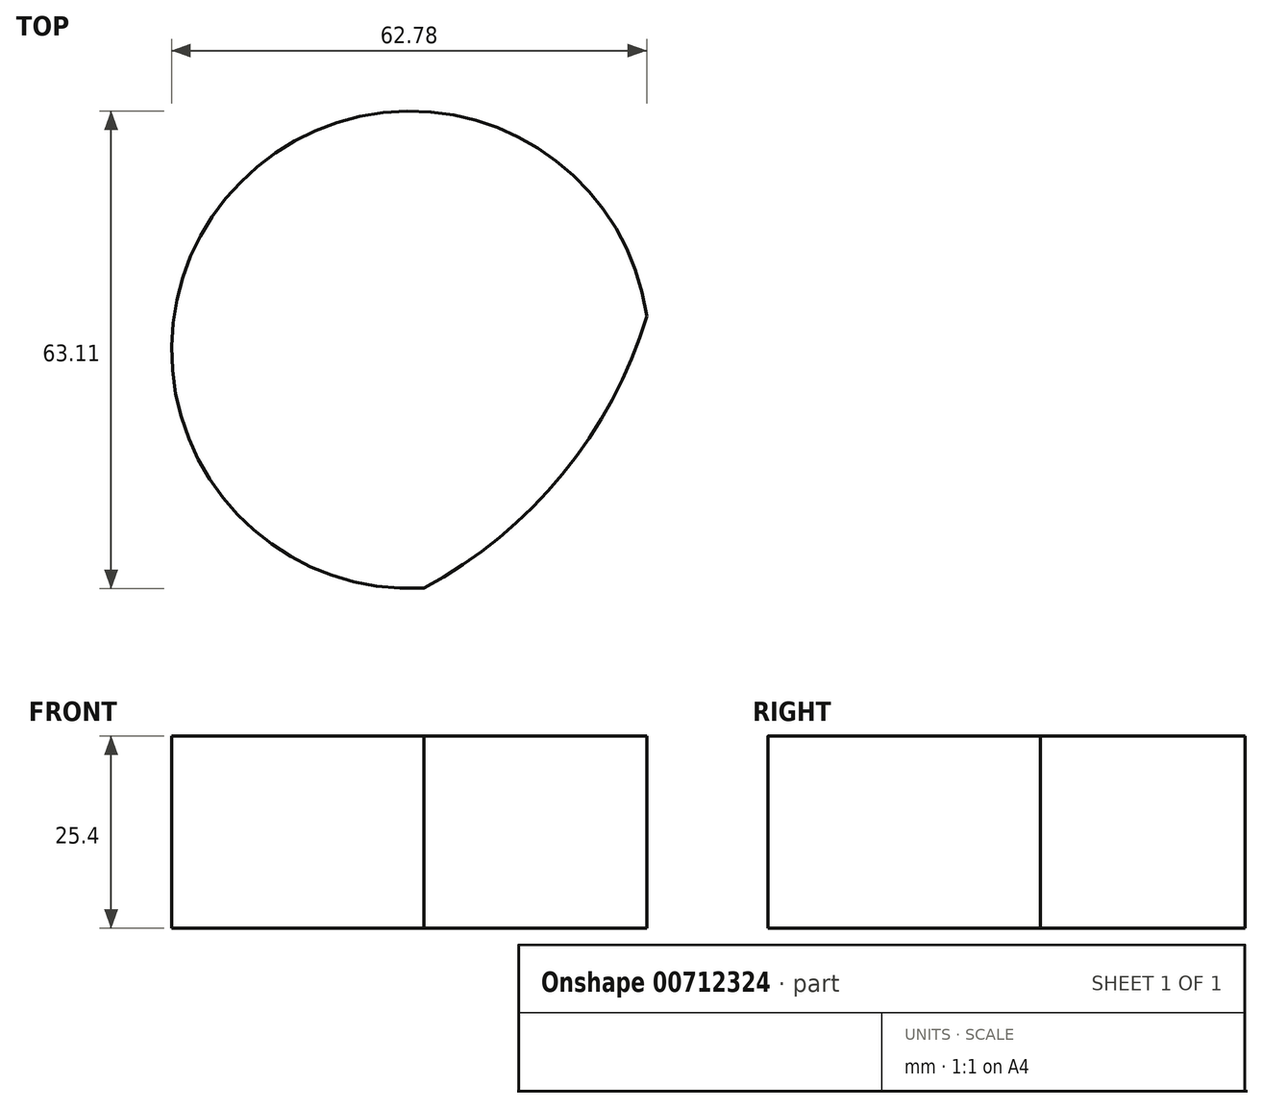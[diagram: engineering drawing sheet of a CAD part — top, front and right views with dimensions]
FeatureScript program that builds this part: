
annotation { "Feature Type Name" : "Feature", "Feature Type Description" : "" }
export const myFeature = defineFeature(function(context is Context, id is Id, definition is map)
    precondition{}
    {
        {
            var Q0;
            Q0=qCreatedBy(makeId("Top.planeOp"),FACE);
            var sketch = newSketch(context, id + "F0", { "sketchPlane" : qUnion([Q0])});
            skCircle(sketch, "E0", {"center": v(0, 0) * mm, "radius": 60.73 * mm});
            skCircle(sketch, "E1", {"center": v(26.9, -22.02) * mm, "radius": 31.55 * mm});
            skCircle(sketch, "E2", {"center": v(0, 0) * mm, "radius": 3.22 * mm});
            skSolve(sketch);
        }
        {
            var Q0;
            {var subQ0=sQuery(id+"F0.wireOp",EDGE,"E1");var subQ1=sQuery(id+"F0.wireOp",EDGE,"E0");var subQ2=makeQuery(id+"F0.imprint","INTERSECT",VERTEX,{"disambiguationData":[OD(0.0)],"derivedFrom":[subQ1,subQ0]});Q0=makeQuery(id+"F0.imprint","IMPRINT",FACE,{"disambiguationData":[TD([[makeQuery(id+"F0.imprint","IMPRINT",EDGE,{"disambiguationData":[TD([[subQ2,1.0]])],"derivedFrom":subQ1}),1.0]])]});}
            extrude(context, id + "F1", {"entities" : qUnion([Q0]), "depth" : 25.4 * mm, "offsetDistance" : 25.4 * mm});
        }
    });
